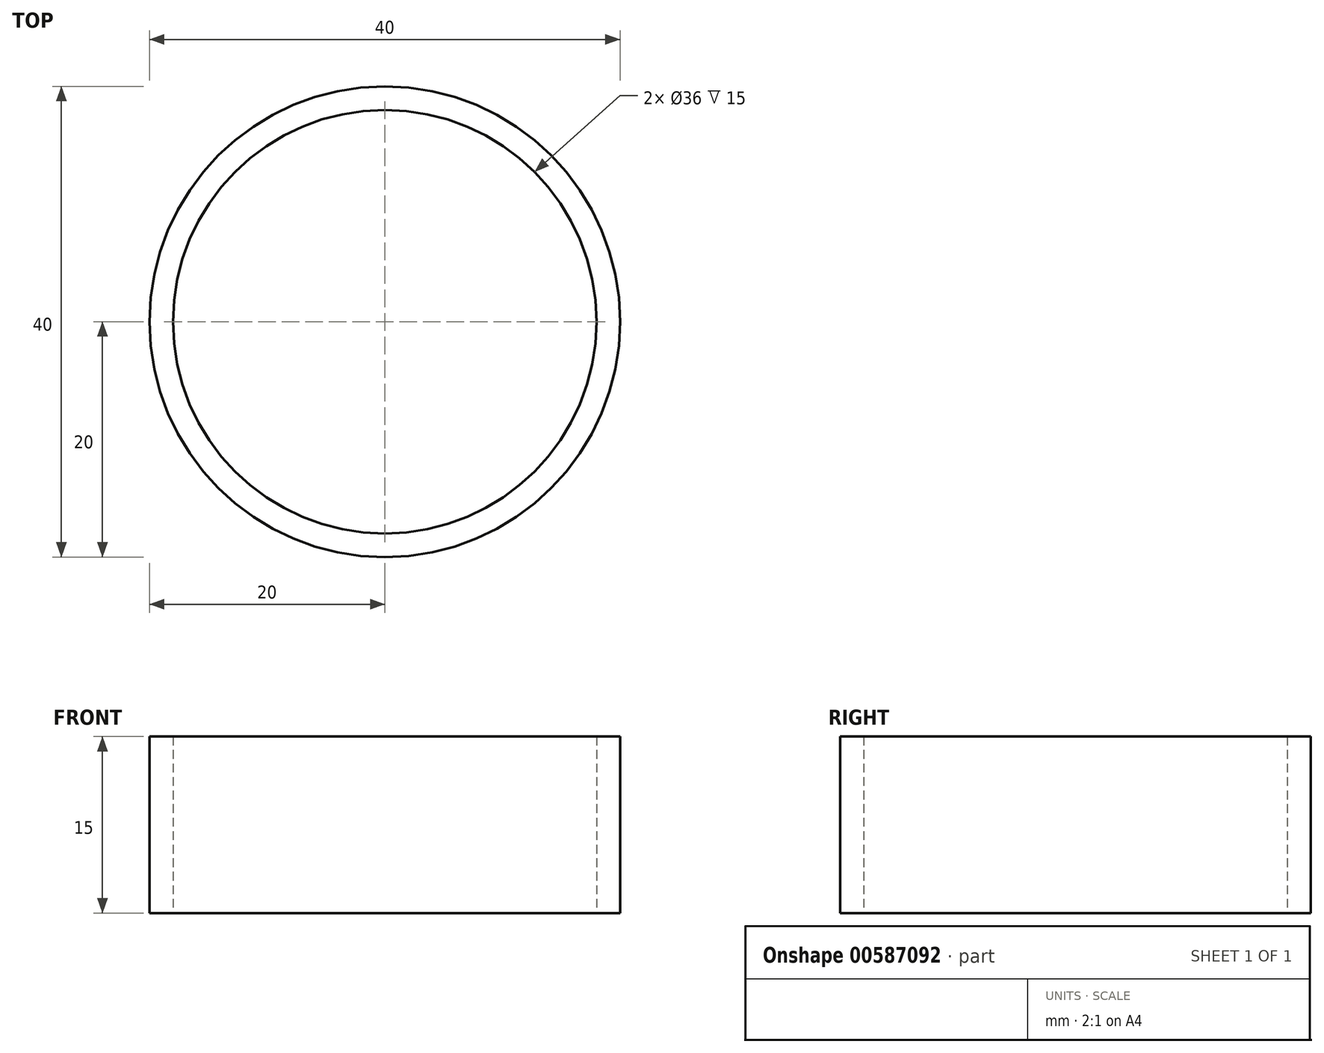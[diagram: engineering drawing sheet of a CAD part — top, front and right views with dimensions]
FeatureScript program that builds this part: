
annotation { "Feature Type Name" : "Feature", "Feature Type Description" : "" }
export const myFeature = defineFeature(function(context is Context, id is Id, definition is map)
    precondition{}
    {
        {
            var Q0;
            Q0=qCreatedBy(makeId("Top.planeOp"),FACE);
            var sketch = newSketch(context, id + "F0", { "sketchPlane" : qUnion([Q0])});
            skCircle(sketch, "E0", {"center": v(0, 0) * mm, "radius": 20 * mm});
            skCircle(sketch, "E1", {"center": v(0, 0) * mm, "radius": 18 * mm});
            skSolve(sketch);
        }
        {
            var Q0;
            Q0=qSketchRegion(id+"F0",true);
            extrude(context, id + "F1", {"entities" : qUnion([Q0]), "depth" : 15 * mm, "offsetDistance" : 25 * mm});
        }
    });
